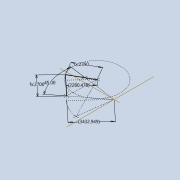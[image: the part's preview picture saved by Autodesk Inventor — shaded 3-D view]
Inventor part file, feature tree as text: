
AUTODESK INVENTOR PART (.ipt)
format: ipt  version: 2022 (Build 260153000, 153)  size: 95,232 bytes
history: native  units: mm
features: sketch x3
ambient origin geometry x8: Origin, YZ Plane, XZ Plane, XY Plane, X Axis, Y Axis, Z Axis, Center Point
feature tree (3):
  sketch  "Sketch1"  dims[d16=2650.0mm]
  sketch  "Sketch4"  dims[d17=900.0mm]
  sketch  "Sketch5"  dims[d18=3450.0mm d19=450.0mm d23=90.0deg d26=2700.0mm d27=2390.0mm d28=2.741281mm d29=5.979373mm d31=2663.899674mm d32=3448.992116mm d33=45.0deg d35=2700.0mm d36=2390.0mm d37=3432.949064mm d38=1319.613411mm d39=800.997403mm d40=2280.47763mm]
